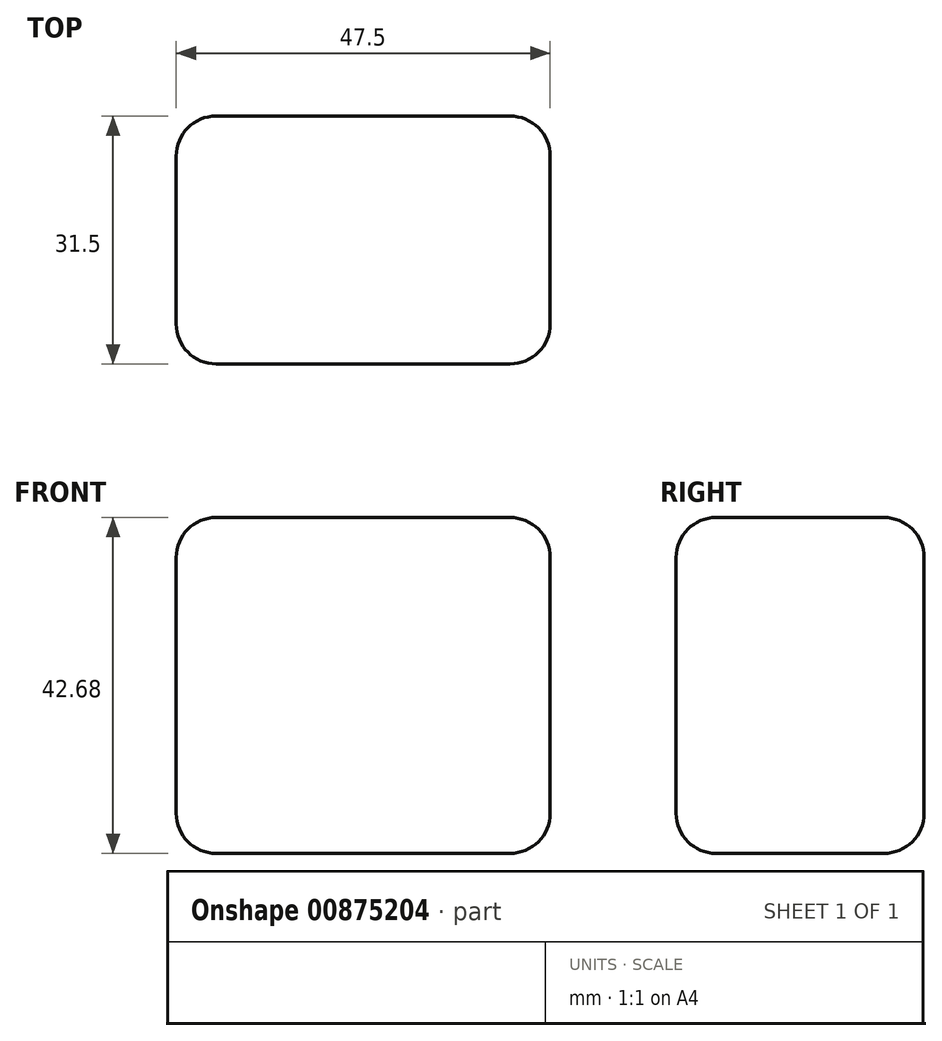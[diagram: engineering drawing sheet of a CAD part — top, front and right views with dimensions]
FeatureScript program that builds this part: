
annotation { "Feature Type Name" : "Feature", "Feature Type Description" : "" }
export const myFeature = defineFeature(function(context is Context, id is Id, definition is map)
    precondition{}
    {
        {
            var Q0;
            Q0=qCreatedBy(makeId("Front.planeOp"),FACE);
            var sketch = newSketch(context, id + "F0", { "sketchPlane" : qUnion([Q0])});
            skLineSegment(sketch, "E0.bottom", {"start": v(-23.75, 21.34) * mm, "end": v(23.75, 21.34) * mm});
            skLineSegment(sketch, "E0.top", {"start": v(-23.75, -21.34) * mm, "end": v(23.75, -21.34) * mm});
            skLineSegment(sketch, "E0.left", {"start": v(-23.75, 21.34) * mm, "end": v(-23.75, -21.34) * mm});
            skLineSegment(sketch, "E0.right", {"start": v(23.75, 21.34) * mm, "end": v(23.75, -21.34) * mm});
            skPoint(sketch, "E0.middle", {"position": v(0, 0) * mm});
            skSolve(sketch);
        }
        {
            var Q0;
            Q0 = qSketchRegion(id + "F0", true);
            extrude(context, id + "F1", {"entities" : qUnion([Q0]), "depth" : 31.5 * mm, "offsetDistance" : 25.4 * mm});
        }
        {
            var Q0;
            Q0=makeQuery(id+"F1.opExtrude","SWEPT_FACE",FACE,{"disambiguationData":[OSD([sQuery(id+"F0.wireOp",EDGE,"E0.left")])]});
            var Q1;
            Q1=makeQuery(id+"F1.opExtrude","SWEPT_FACE",FACE,{"disambiguationData":[OSD([sQuery(id+"F0.wireOp",EDGE,"E0.bottom")])]});
            var Q2;
            Q2=makeQuery(id+"F1.opExtrude","CAP_FACE",FACE,{"disambiguationData":[OSD([sQuery(id+"F0.wireOp",EDGE,"E0.bottom"),sQuery(id+"F0.wireOp",EDGE,"E0.top"),sQuery(id+"F0.wireOp",EDGE,"E0.left"),sQuery(id+"F0.wireOp",EDGE,"E0.right")])],"isStart":true});
            var Q3;
            Q3=makeQuery(id+"F1.opExtrude","SWEPT_FACE",FACE,{"disambiguationData":[OSD([sQuery(id+"F0.wireOp",EDGE,"E0.right")])]});
            var Q4;
            Q4=makeQuery(id+"F1.opExtrude","CAP_FACE",FACE,{"disambiguationData":[OSD([sQuery(id+"F0.wireOp",EDGE,"E0.bottom"),sQuery(id+"F0.wireOp",EDGE,"E0.top"),sQuery(id+"F0.wireOp",EDGE,"E0.left"),sQuery(id+"F0.wireOp",EDGE,"E0.right")])],"isStart":false});
            fillet(context, id + "F2", {"entities" : qUnion([Q0, Q1, Q2, Q3, Q4]), "radius" : 5.08 * mm, "tangentPropagation" : true, "allowEdgeOverflow" : false});
        }
    });
